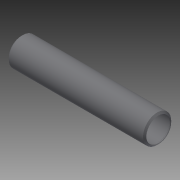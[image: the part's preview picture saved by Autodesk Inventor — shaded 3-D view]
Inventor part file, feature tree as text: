
AUTODESK INVENTOR PART (.ipt)
format: ipt  version: 2014 (Build 180170000, 170)  size: 121,344 bytes
history: native  units: in
note: dims shown in document units (in); Inventor stores cm internally (conversion verified against a paired STEP export)
features: other x56, revolve x1, sketch x1
ambient origin geometry x8: Origin, YZ Plane, XZ Plane, XY Plane, X Axis, Y Axis, Z Axis, Center Point
bodies: Solid1 (feature_tree)
feature tree (58):
  revolve  "Revolution1"  [1 undecoded]
  other  "o1_XY"
  other  "o1_YZ"
  other  "o1_ZX"
  other  "o1_X"
  other  "o1_Y"
  other  "o1_Z"
  other  "o1_Center"
  other  "o2_XY"
  other  "o2_YZ"
  other  "o2_ZX"
  other  "o2_X"
  other  "o2_Y"
  other  "o2_Z"
  other  "o2_Center"
  other  "t1_XY"
  other  "t1_YZ"
  other  "t1_ZX"
  other  "t1_X"
  other  "t1_Y"
  other  "t1_Z"
  other  "t1_Center"
  other  "t2_XY"
  other  "t2_YZ"
  other  "t2_ZX"
  other  "t2_X"
  other  "t2_Y"
  other  "t2_Z"
  other  "t2_Center"
  other  "t3_XY"
  other  "t3_YZ"
  other  "t3_ZX"
  other  "t3_X"
  other  "t3_Y"
  other  "t3_Z"
  other  "t3_Center"
  other  "t4_XY"
  other  "t4_YZ"
  other  "t4_ZX"
  other  "t4_X"
  other  "t4_Y"
  other  "t4_Z"
  other  "t4_Center"
  other  "tube1_XY"
  other  "tube1_YZ"
  other  "tube1_ZX"
  other  "tube1_X"
  other  "tube1_Y"
  other  "tube1_Z"
  other  "tube1_Center"
  other  "tube2_XY"
  other  "tube2_YZ"
  other  "tube2_ZX"
  other  "tube2_X"
  other  "tube2_Y"
  other  "tube2_Z"
  other  "tube2_Center"
  sketch  "Sketch_5"  dims[d0=360.0deg]
note: 1 required parameter value undecoded (feature->parameter linkage not recoverable at this tier; creation-order binding heuristic only, values carry confidence <= 0.55)
